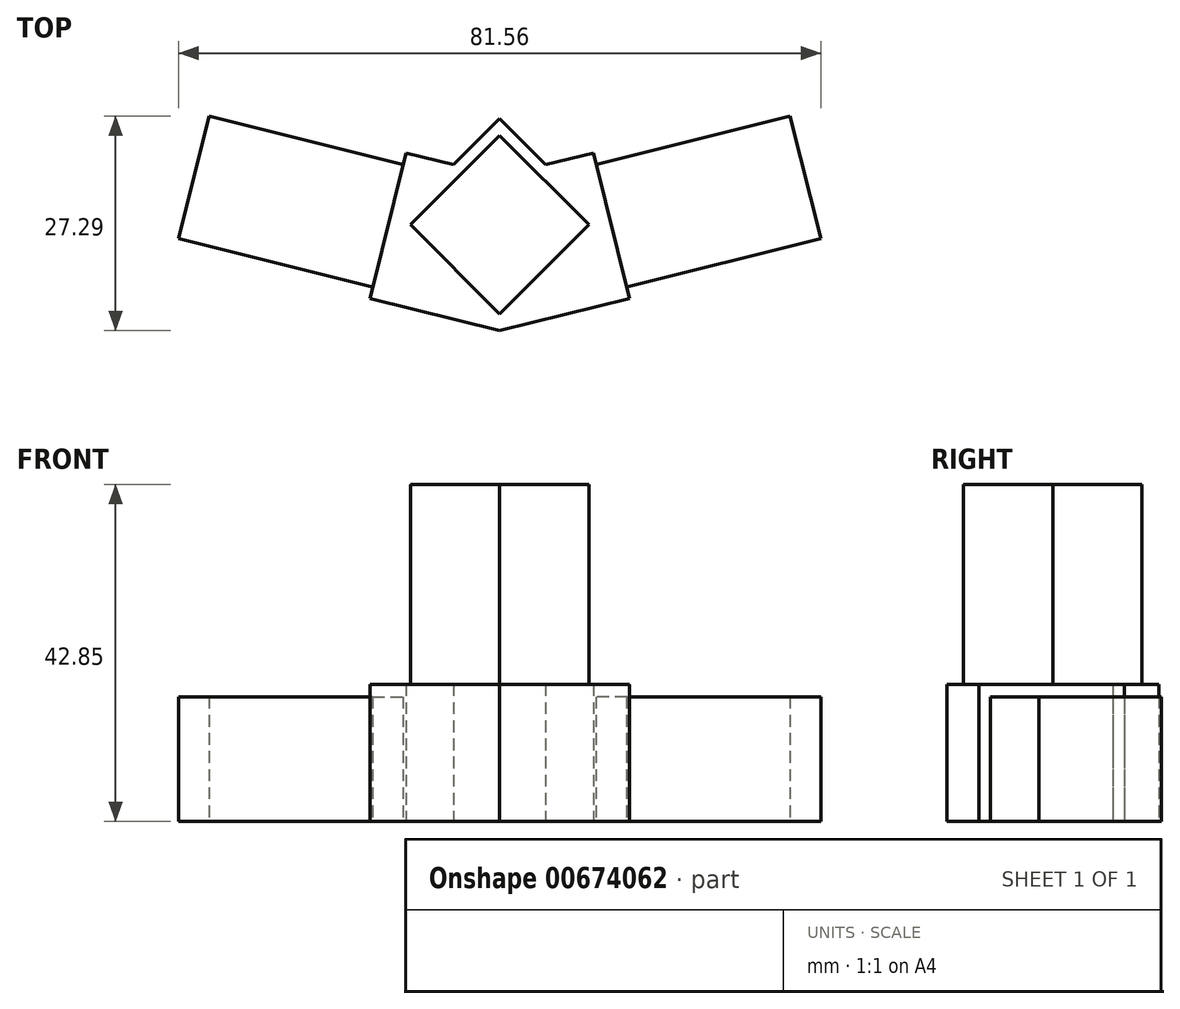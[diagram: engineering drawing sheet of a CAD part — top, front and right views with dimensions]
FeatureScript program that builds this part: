
annotation { "Feature Type Name" : "Feature", "Feature Type Description" : "" }
export const myFeature = defineFeature(function(context is Context, id is Id, definition is map)
    precondition{}
    {
        {
            var Q0;
            Q0=qCreatedBy(makeId("Top.planeOp"),FACE);
            var sketch = newSketch(context, id + "F0", { "sketchPlane" : qUnion([Q0])});
            skLineSegment(sketch, "E0", {"start": v(0, 0) * mm, "end": v(16.5, 4.11) * mm});
            skLineSegment(sketch, "E1", {"start": v(16.5, 4.11) * mm, "end": v(16.13, 5.57) * mm});
            skLineSegment(sketch, "E2", {"start": v(16.13, 5.57) * mm, "end": v(40.78, 11.71) * mm});
            skLineSegment(sketch, "E3", {"start": v(40.78, 11.71) * mm, "end": v(36.9, 27.29) * mm});
            skLineSegment(sketch, "E4", {"start": v(36.9, 27.29) * mm, "end": v(12.25, 21.14) * mm});
            skLineSegment(sketch, "E5", {"start": v(12.25, 21.14) * mm, "end": v(11.89, 22.6) * mm});
            skLineSegment(sketch, "E6", {"start": v(11.89, 22.6) * mm, "end": v(5.85, 21.1) * mm});
            skLineSegment(sketch, "E7", {"start": v(0, 0) * mm, "end": v(13.47, 13.47) * mm, "construction": true});
            skLineSegment(sketch, "E8", {"start": v(13.47, 13.47) * mm, "end": v(0, 26.94) * mm, "construction": true});
            skPoint(sketch, "E9.orphan", {"position": v(0, 19.63) * mm});
            skLineSegment(sketch, "E10", {"start": v(0, 26.94) * mm, "end": v(5.85, 21.1) * mm});
            skLineSegment(sketch, "E11.MirrorCS", {"start": v(-11.89, 22.6) * mm, "end": v(-5.85, 21.1) * mm});
            skLineSegment(sketch, "E12.MirrorCS", {"start": v(0, 0) * mm, "end": v(-16.5, 4.11) * mm});
            skLineSegment(sketch, "E13.MirrorCS", {"start": v(-16.5, 4.11) * mm, "end": v(-16.13, 5.57) * mm});
            skLineSegment(sketch, "E14.MirrorCS", {"start": v(-16.13, 5.57) * mm, "end": v(-40.78, 11.71) * mm});
            skLineSegment(sketch, "E15.MirrorCS", {"start": v(-12.25, 21.14) * mm, "end": v(-11.89, 22.6) * mm});
            skLineSegment(sketch, "E16.MirrorCS", {"start": v(-36.9, 27.29) * mm, "end": v(-12.25, 21.14) * mm});
            skLineSegment(sketch, "E17.MirrorCS", {"start": v(-40.78, 11.71) * mm, "end": v(-36.9, 27.29) * mm});
            skLineSegment(sketch, "E18.MirrorCS", {"start": v(0, 26.94) * mm, "end": v(-5.85, 21.1) * mm});
            skSolve(sketch);
        }
        {
            var Q0;
            Q0=makeQuery(id+"F0.imprint","IMPRINT",FACE,{"disambiguationData":[TD([[makeQuery(id+"F0.imprint","IMPRINT",EDGE,{"derivedFrom":sQuery(id+"F0.wireOp",EDGE,"E0")}),1.0]])]});
            extrude(context, id + "F1", {"entities" : qUnion([Q0]), "depth" : 15.85 * mm, "offsetDistance" : 25 * mm});
        }
        {
            var Q0;
            Q0=makeQuery(id+"F1.opExtrude","CAP_FACE",FACE,{"disambiguationData":[OSD([sQuery(id+"F0.wireOp",EDGE,"E0"),sQuery(id+"F0.wireOp",EDGE,"E1"),sQuery(id+"F0.wireOp",EDGE,"E2"),sQuery(id+"F0.wireOp",EDGE,"E3"),sQuery(id+"F0.wireOp",EDGE,"E4"),sQuery(id+"F0.wireOp",EDGE,"E5"),sQuery(id+"F0.wireOp",EDGE,"E6"),sQuery(id+"F0.wireOp",EDGE,"E10"),sQuery(id+"F0.wireOp",EDGE,"E11.MirrorCS"),sQuery(id+"F0.wireOp",EDGE,"E12.MirrorCS"),sQuery(id+"F0.wireOp",EDGE,"E13.MirrorCS"),sQuery(id+"F0.wireOp",EDGE,"E14.MirrorCS"),sQuery(id+"F0.wireOp",EDGE,"E15.MirrorCS"),sQuery(id+"F0.wireOp",EDGE,"E16.MirrorCS"),sQuery(id+"F0.wireOp",EDGE,"E17.MirrorCS"),sQuery(id+"F0.wireOp",EDGE,"E18.MirrorCS")])],"isStart":false});
            var sketch = newSketch(context, id + "F2", { "sketchPlane" : qUnion([Q0])});
            skLineSegment(sketch, "E19", {"start": v(-16.5, 4.11) * mm, "end": v(0, 0) * mm});
            skLineSegment(sketch, "E20", {"start": v(0, 0) * mm, "end": v(16.5, 4.11) * mm});
            skLineSegment(sketch, "E21", {"start": v(16.5, 4.11) * mm, "end": v(11.89, 22.6) * mm});
            skLineSegment(sketch, "E22", {"start": v(11.89, 22.6) * mm, "end": v(5.85, 21.1) * mm});
            skLineSegment(sketch, "E23", {"start": v(5.85, 21.1) * mm, "end": v(0, 26.94) * mm});
            skLineSegment(sketch, "E24", {"start": v(0, 26.94) * mm, "end": v(-5.85, 21.1) * mm});
            skLineSegment(sketch, "E25", {"start": v(-5.85, 21.1) * mm, "end": v(-11.89, 22.6) * mm});
            skLineSegment(sketch, "E26", {"start": v(-11.89, 22.6) * mm, "end": v(-16.5, 4.11) * mm});
            skSolve(sketch);
        }
        {
            var Q0;
            {var subQ7=sQuery(id+"F2.wireOp",EDGE,"E19");Q0=makeQuery(id+"F2.imprint","IMPRINT",FACE,{"disambiguationData":[TD([[makeQuery(id+"F2.imprint","IMPRINT",EDGE,{"derivedFrom":subQ7}),-1.0]])]});}
            extrude(context, id + "F3", {"entities" : qUnion([Q0]), "operationType" : NewBodyOperationType.ADD, "depth" : 1.6 * mm, "offsetDistance" : 25 * mm});
        }
        {
            var Q0;
            Q0=makeQuery(id+"F3.opExtrude","CAP_FACE",FACE,{"disambiguationData":[OSD([sQuery(id+"F2.wireOp",EDGE,"E19"),sQuery(id+"F2.wireOp",EDGE,"E20"),sQuery(id+"F2.wireOp",EDGE,"E21"),sQuery(id+"F2.wireOp",EDGE,"E22"),sQuery(id+"F2.wireOp",EDGE,"E23"),sQuery(id+"F2.wireOp",EDGE,"E24"),sQuery(id+"F2.wireOp",EDGE,"E25"),sQuery(id+"F2.wireOp",EDGE,"E26")])],"isStart":false});
            var sketch = newSketch(context, id + "F4", { "sketchPlane" : qUnion([Q0])});
            skLineSegment(sketch, "E27.0", {"start": v(0, 0) * mm, "end": v(13.47, 13.47) * mm, "construction": true});
            skLineSegment(sketch, "E28.0", {"start": v(13.47, 13.47) * mm, "end": v(0, 26.94) * mm, "construction": true});
            skLineSegment(sketch, "E29", {"start": v(0, 2.12) * mm, "end": v(11.35, 13.47) * mm});
            skLineSegment(sketch, "E30", {"start": v(11.35, 13.47) * mm, "end": v(0, 24.82) * mm});
            skLineSegment(sketch, "E31.MirrorCS", {"start": v(-11.35, 13.47) * mm, "end": v(0, 24.82) * mm});
            skLineSegment(sketch, "E32.MirrorCS", {"start": v(0, 2.12) * mm, "end": v(-11.35, 13.47) * mm});
            skSolve(sketch);
        }
        {
            var Q0;
            Q0=makeQuery(id+"F4.imprint","IMPRINT",FACE,{"disambiguationData":[TD([[makeQuery(id+"F4.imprint","IMPRINT",EDGE,{"derivedFrom":sQuery(id+"F4.wireOp",EDGE,"E29")}),1.0]])]});
            extrude(context, id + "F5", {"entities" : qUnion([Q0]), "operationType" : NewBodyOperationType.ADD, "depth" : 25.4 * mm, "offsetDistance" : 25 * mm});
        }
    });
